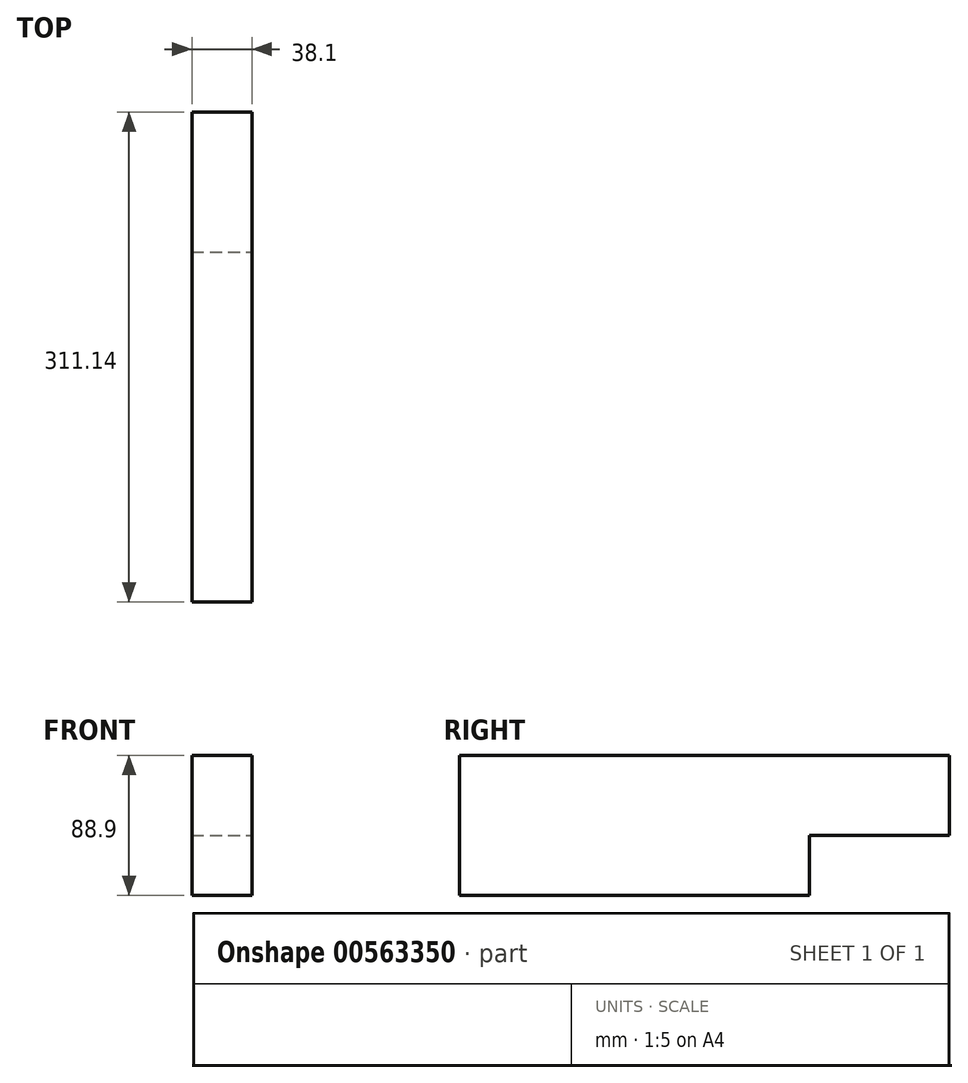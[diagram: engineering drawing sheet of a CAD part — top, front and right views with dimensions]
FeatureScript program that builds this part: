
annotation { "Feature Type Name" : "Feature", "Feature Type Description" : "" }
export const myFeature = defineFeature(function(context is Context, id is Id, definition is map)
    precondition{}
    {
        {
            var Q0;
            Q0=qCreatedBy(makeId("Top.planeOp"),FACE);
            var sketch = newSketch(context, id + "F0", { "sketchPlane" : qUnion([Q0])});
            skLineSegment(sketch, "E0.bottom", {"start": v(-19.05, -155.58) * mm, "end": v(19.05, -155.58) * mm});
            skLineSegment(sketch, "E0.top", {"start": v(-19.05, 155.58) * mm, "end": v(19.05, 155.58) * mm});
            skLineSegment(sketch, "E0.left", {"start": v(-19.05, -155.58) * mm, "end": v(-19.05, 155.58) * mm});
            skLineSegment(sketch, "E0.right", {"start": v(19.05, -155.58) * mm, "end": v(19.05, 155.58) * mm});
            skPoint(sketch, "E0.middle", {"position": v(0, 0) * mm});
            skLineSegment(sketch, "E1", {"start": v(-19.05, 66.67) * mm, "end": v(19.05, 66.67) * mm});
            skSolve(sketch);
        }
        {
            var Q0;
            {var subQ0=sQuery(id+"F0.wireOp",EDGE,"E0.bottom");Q0=makeQuery(id+"F0.imprint","IMPRINT",FACE,{"disambiguationData":[TD([[makeQuery(id+"F0.imprint","IMPRINT",EDGE,{"derivedFrom":subQ0}),1.0]])]});}
            extrude(context, id + "F1", {"entities" : qUnion([Q0]), "oppositeDirection" : true, "depth" : 88.9 * mm, "offsetDistance" : 25.4 * mm});
        }
        {
            var Q0;
            {var subQ0=sQuery(id+"F0.wireOp",EDGE,"E0.top");Q0=makeQuery(id+"F0.imprint","IMPRINT",FACE,{"disambiguationData":[TD([[makeQuery(id+"F0.imprint","IMPRINT",EDGE,{"derivedFrom":subQ0}),-1.0]])]});}
            extrude(context, id + "F2", {"entities" : qUnion([Q0]), "operationType" : NewBodyOperationType.ADD, "oppositeDirection" : true, "depth" : 50.8 * mm, "offsetDistance" : 25.4 * mm});
        }
    });
